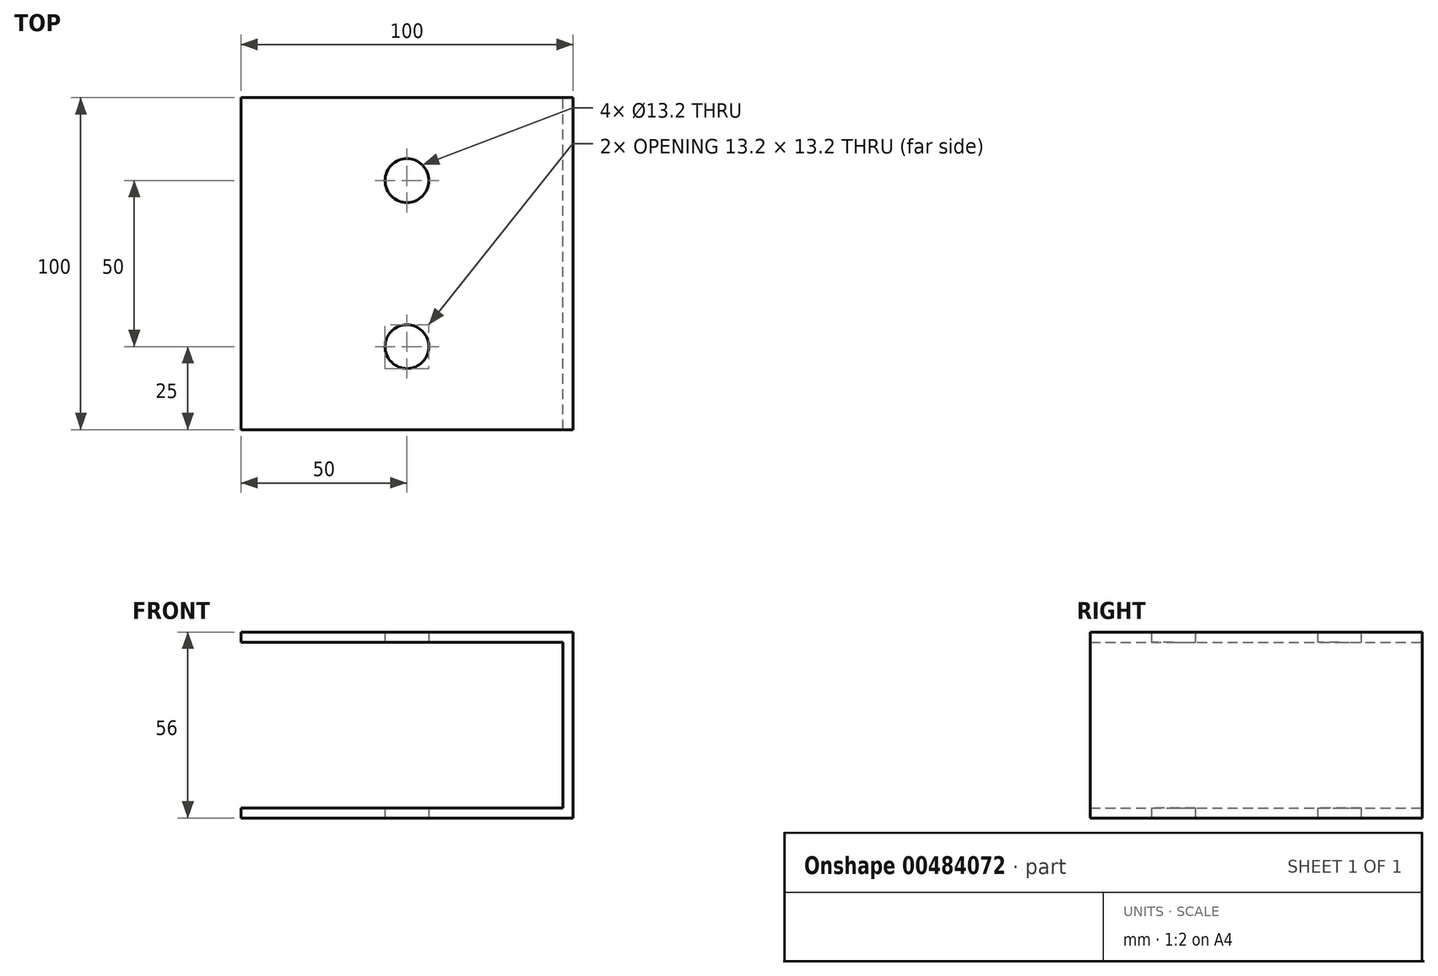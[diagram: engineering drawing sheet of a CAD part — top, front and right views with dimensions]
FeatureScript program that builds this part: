
annotation { "Feature Type Name" : "Feature", "Feature Type Description" : "" }
export const myFeature = defineFeature(function(context is Context, id is Id, definition is map)
    precondition{}
    {
        {
            var Q0;
            Q0=qCreatedBy(makeId("Front.planeOp"),FACE);
            var sketch = newSketch(context, id + "F0", { "sketchPlane" : qUnion([Q0])});
            skLineSegment(sketch, "E0", {"start": v(0, 0) * mm, "end": v(0, 56) * mm});
            skLineSegment(sketch, "E1", {"start": v(0, 56) * mm, "end": v(-100, 56) * mm});
            skLineSegment(sketch, "E2", {"start": v(-100, 56) * mm, "end": v(-100, 53) * mm});
            skLineSegment(sketch, "E3", {"start": v(-100, 53) * mm, "end": v(-3, 53) * mm});
            skLineSegment(sketch, "E4", {"start": v(-3, 53) * mm, "end": v(-3, 3) * mm});
            skLineSegment(sketch, "E5", {"start": v(-3, 3) * mm, "end": v(-100, 3) * mm});
            skLineSegment(sketch, "E6", {"start": v(-100, 3) * mm, "end": v(-100, 0) * mm});
            skLineSegment(sketch, "E7", {"start": v(-100, 0) * mm, "end": v(0, 0) * mm});
            skSolve(sketch);
        }
        {
            var Q0;
            Q0 = qSketchRegion(id + "F0", true);
            extrude(context, id + "F1", {"entities" : qUnion([Q0]), "depth" : 100 * mm});
        }
        {
            var Q0;
            Q0=makeQuery(id+"F1.opExtrude","SWEPT_FACE",FACE,{"disambiguationData":[OSD([sQuery(id+"F0.wireOp",EDGE,"E1")])]});
            var sketch = newSketch(context, id + "F2", { "sketchPlane" : qUnion([Q0])});
            skLineSegment(sketch, "E8", {"start": v(-50, -100) * mm, "end": v(-50, 0) * mm});
            skLineSegment(sketch, "E9", {"start": v(-50, -100) * mm, "end": v(-50, -75) * mm});
            skLineSegment(sketch, "E10", {"start": v(-50, 0) * mm, "end": v(-50, -25) * mm});
            skSolve(sketch);
        }
        {
            var Q0;
            Q0=sQuery(id+"F2.wireOp",VERTEX,"E9.end");
            var Q1;
            Q1=sQuery(id+"F2.wireOp",VERTEX,"E10.end");
            var Q2;
            Q2=makeQuery(id+"F1.opExtrude","SWEPT_BODY",BODY,{"disambiguationData":[OSD([sQuery(id+"F0.wireOp",EDGE,"E0"),sQuery(id+"F0.wireOp",EDGE,"E1"),sQuery(id+"F0.wireOp",EDGE,"E2"),sQuery(id+"F0.wireOp",EDGE,"E3"),sQuery(id+"F0.wireOp",EDGE,"E4"),sQuery(id+"F0.wireOp",EDGE,"E5"),sQuery(id+"F0.wireOp",EDGE,"E6"),sQuery(id+"F0.wireOp",EDGE,"E7")])]});
            hole(context, id + "F3", {"style" : HoleStyle.SIMPLE, "endStyle" : HoleEndStyle.THROUGH, "standardTappedOrClearance" : lookupTablePath({ "standard" : "ISO", "fit" : "Normal", "size" : "M12", "type" : "Clearance" }), "standardBlindInLast" : lookupTablePath({ "fit" : "Standard", "standard" : "ISO", "size" : "M12", "type" : "Clearance" }), "holeDiameter" : 13.2 * mm, "isTappedThrough" : true, "tappedDepth" : 12 * mm, "tapClearance" : 3, "locations" : qUnion([Q0, Q1]), "scope" : qUnion([Q2])});
        }
    });
